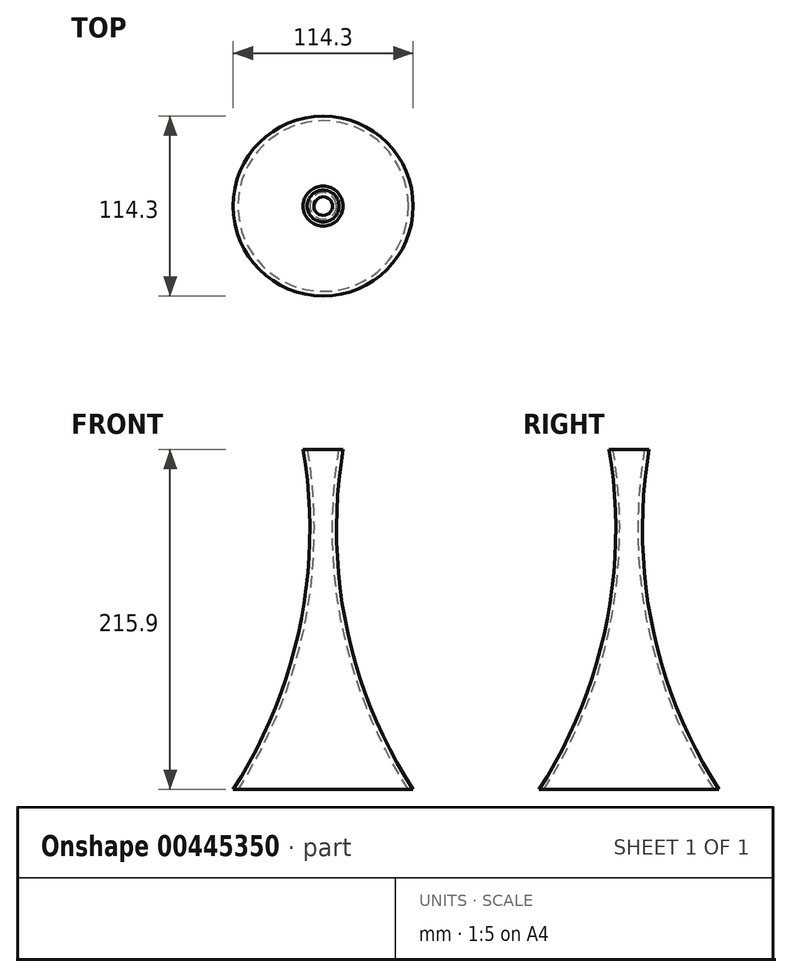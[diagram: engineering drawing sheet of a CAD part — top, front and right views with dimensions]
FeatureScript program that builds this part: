
annotation { "Feature Type Name" : "Feature", "Feature Type Description" : "" }
export const myFeature = defineFeature(function(context is Context, id is Id, definition is map)
    precondition{}
    {
        {
            var Q0;
            Q0=qCreatedBy(makeId("Front.planeOp"),FACE);
            var sketch = newSketch(context, id + "F0", { "sketchPlane" : qUnion([Q0])});
            skLineSegment(sketch, "E0", {"start": v(-24.97, 94.72) * mm, "end": v(-24.97, -121.18) * mm});
            skLineSegment(sketch, "E1", {"start": v(-24.97, -121.18) * mm, "end": v(32.18, -121.18) * mm});
            skLineSegment(sketch, "E2", {"start": v(-24.97, 94.72) * mm, "end": v(-12.27, 94.72) * mm});
            skArc(sketch, "E3", {"start": v(-12.27, 94.72) * mm, "mid": v(-10.25, -17.39) * mm, "end": v(32.18, -121.18) * mm});
            skSolve(sketch);
        }
        {
            var Q0;
            Q0=makeQuery(id+"F0.imprint","IMPRINT",FACE,{"disambiguationData":[TD([[makeQuery(id+"F0.imprint","IMPRINT",EDGE,{"derivedFrom":sQuery(id+"F0.wireOp",EDGE,"E0")}),1.0]])]});
            var Q1;
            Q1=sQuery(id+"F0.wireOp",EDGE,"E0");
            revolve(context, id + "F1", {"entities" : qUnion([Q0]), "axis" : qUnion([Q1]), "revolveType" : RevolveType.FULL});
        }
        {
            var Q0;
            Q0=makeQuery(id+"F1.opRevolve","SWEPT_FACE",FACE,{"disambiguationData":[OSD([sQuery(id+"F0.wireOp",EDGE,"E1")])]});
            var Q1;
            Q1=makeQuery(id+"F1.opRevolve","SWEPT_FACE",FACE,{"disambiguationData":[OSD([sQuery(id+"F0.wireOp",EDGE,"E2")])]});
            shell(context, id + "F2", {"entities" : qUnion([Q0, Q1]), "thickness" : 2.54 * mm});
        }
    });
